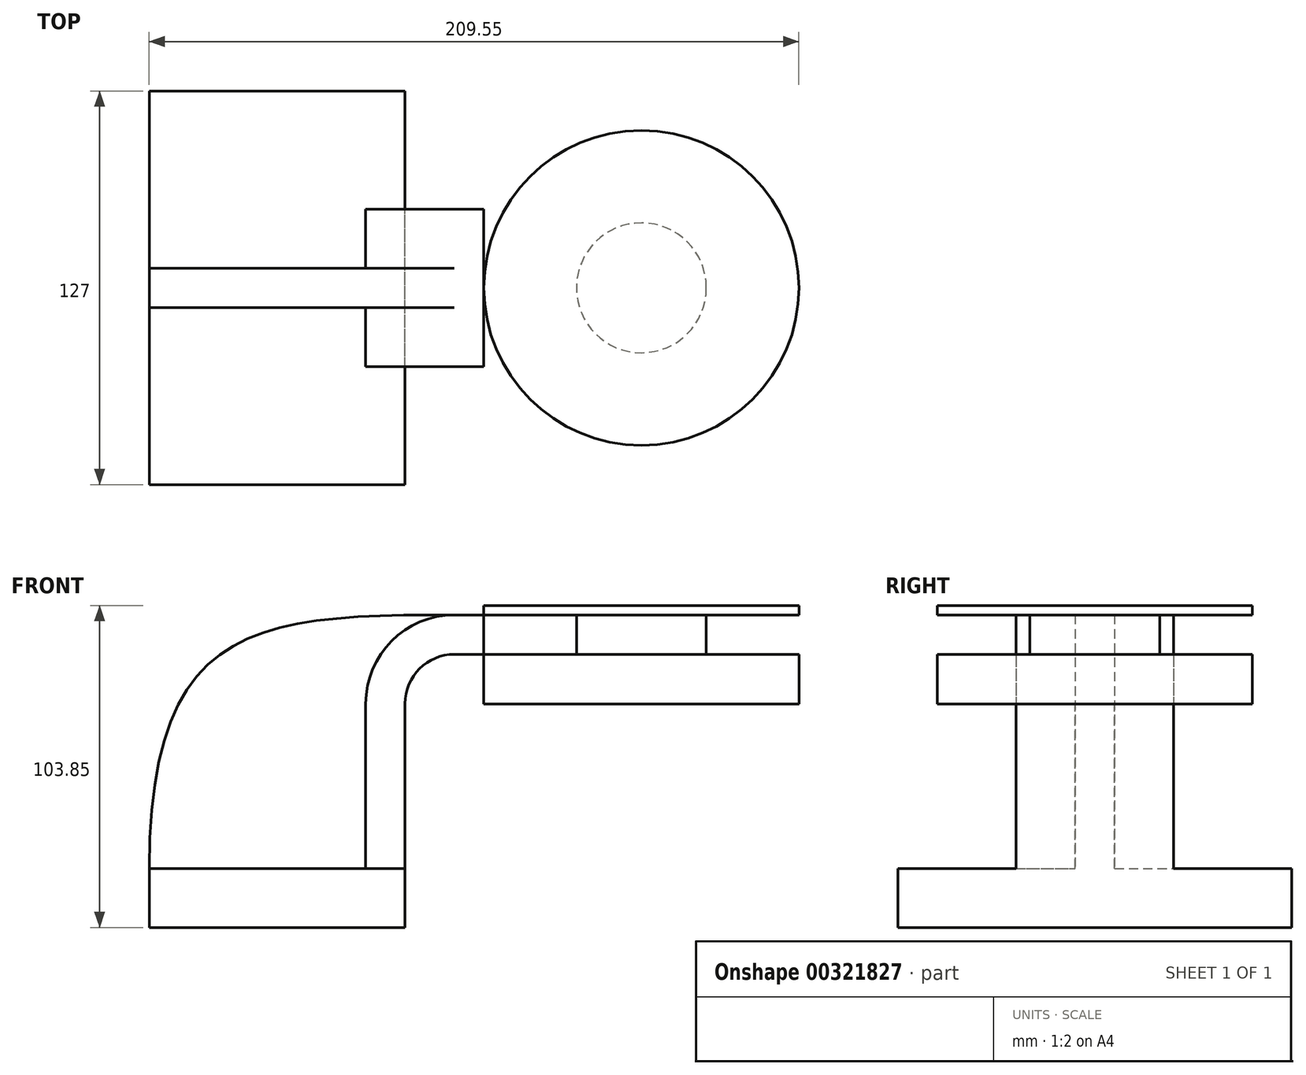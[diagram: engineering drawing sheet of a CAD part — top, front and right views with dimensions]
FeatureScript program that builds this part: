
annotation { "Feature Type Name" : "Feature", "Feature Type Description" : "" }
export const myFeature = defineFeature(function(context is Context, id is Id, definition is map)
    precondition{}
    {
        {
            var Q0;
            Q0=qCreatedBy(makeId("Front.planeOp"),FACE);
            var sketch = newSketch(context, id + "F0", { "sketchPlane" : qUnion([Q0])});
            skLineSegment(sketch, "E0.bottom", {"start": v(-83.58, -57.9) * mm, "end": v(-1.03, -57.9) * mm});
            skLineSegment(sketch, "E0.top", {"start": v(-83.58, -38.86) * mm, "end": v(-1.03, -38.86) * mm});
            skLineSegment(sketch, "E0.left", {"start": v(-83.58, -57.9) * mm, "end": v(-83.58, -38.86) * mm});
            skLineSegment(sketch, "E0.right", {"start": v(-1.03, -57.9) * mm, "end": v(-1.03, -38.86) * mm});
            skLineSegment(sketch, "E1.bottom", {"start": v(24.37, 14.19) * mm, "end": v(75.17, 14.19) * mm});
            skLineSegment(sketch, "E1.top", {"start": v(24.37, 45.94) * mm, "end": v(75.17, 45.94) * mm});
            skLineSegment(sketch, "E1.left", {"start": v(24.37, 14.19) * mm, "end": v(24.37, 45.94) * mm});
            skLineSegment(sketch, "E1.right", {"start": v(75.17, 14.19) * mm, "end": v(75.17, 45.94) * mm});
            skLineSegment(sketch, "E2", {"start": v(-1.03, -38.86) * mm, "end": v(-1.03, 14.33) * mm});
            skPoint(sketch, "E3.endSnap0", {"position": v(24.37, 30.06) * mm});
            skArc(sketch, "E4", {"start": v(-1.03, 14.33) * mm, "mid": v(3.62, 25.55) * mm, "end": v(14.85, 30.2) * mm});
            skLineSegment(sketch, "E5", {"start": v(14.85, 30.2) * mm, "end": v(54.22, 30.2) * mm});
            skLineSegment(sketch, "E6.0", {"start": v(14.85, 42.9) * mm, "end": v(54.22, 42.9) * mm});
            skArc(sketch, "E6.1", {"start": v(-13.73, 14.33) * mm, "mid": v(-5.36, 34.53) * mm, "end": v(14.85, 42.9) * mm});
            skLineSegment(sketch, "E6.2", {"start": v(-13.73, -38.86) * mm, "end": v(-13.73, 14.33) * mm});
            skLineSegment(sketch, "E7", {"start": v(54.22, 42.9) * mm, "end": v(54.22, 30.2) * mm});
            skLineSegment(sketch, "E8", {"start": v(-13.73, -38.86) * mm, "end": v(-1.03, -38.86) * mm});
            skFitSpline(sketch, "E9", {"points": [v(14.85, 42.9) * mm, v(-83.58, -38.86) * mm], "startDerivative": vector(-195.9, 0.83) * mm, "endDerivative": vector(-1.28, -235.2) * mm});
            skSolve(sketch);
        }
        {
            var Q0;
            Q0=makeQuery(id+"F0.imprint","IMPRINT",FACE,{"disambiguationData":[TD([[makeQuery(id+"F0.imprint","IMPRINT",EDGE,{"derivedFrom":sQuery(id+"F0.wireOp",EDGE,"E0.bottom")}),1.0]])]});
            extrude(context, id + "F1", {"entities" : qUnion([Q0]), "endBound" : BoundingType.SYMMETRIC, "depth" : 127 * mm});
        }
        {
            var Q0;
            Q0=makeQuery(id+"F0.imprint","IMPRINT",FACE,{"disambiguationData":[TD([[makeQuery(id+"F0.imprint","IMPRINT",EDGE,{"derivedFrom":sQuery(id+"F0.wireOp",EDGE,"E2")}),1.0]])]});
            extrude(context, id + "F2", {"entities" : qUnion([Q0]), "operationType" : NewBodyOperationType.ADD, "endBound" : BoundingType.SYMMETRIC, "depth" : 50.8 * mm});
        }
        {
            var Q0;
            Q0=makeQuery(id+"F0.imprint","IMPRINT",FACE,{"disambiguationData":[TD([[makeQuery(id+"F0.imprint","IMPRINT",EDGE,{"derivedFrom":sQuery(id+"F0.wireOp",EDGE,"E0.top")}),1.0]])]});
            extrude(context, id + "F3", {"entities" : qUnion([Q0]), "operationType" : NewBodyOperationType.ADD, "endBound" : BoundingType.SYMMETRIC, "depth" : 12.7 * mm});
        }
        {
            var Q0;
            {var subQ4=sQuery(id+"F0.wireOp",EDGE,"E1.bottom");Q0=makeQuery(id+"F0.imprint","IMPRINT",FACE,{"disambiguationData":[TD([[makeQuery(id+"F0.imprint","IMPRINT",EDGE,{"derivedFrom":subQ4}),1.0]])]});}
            var Q1;
            Q1=sQuery(id+"F0.wireOp",EDGE,"E1.right");
            revolve(context, id + "F4", {"entities" : qUnion([Q0]), "axis" : qUnion([Q1]), "revolveType" : RevolveType.FULL});
        }
    });
